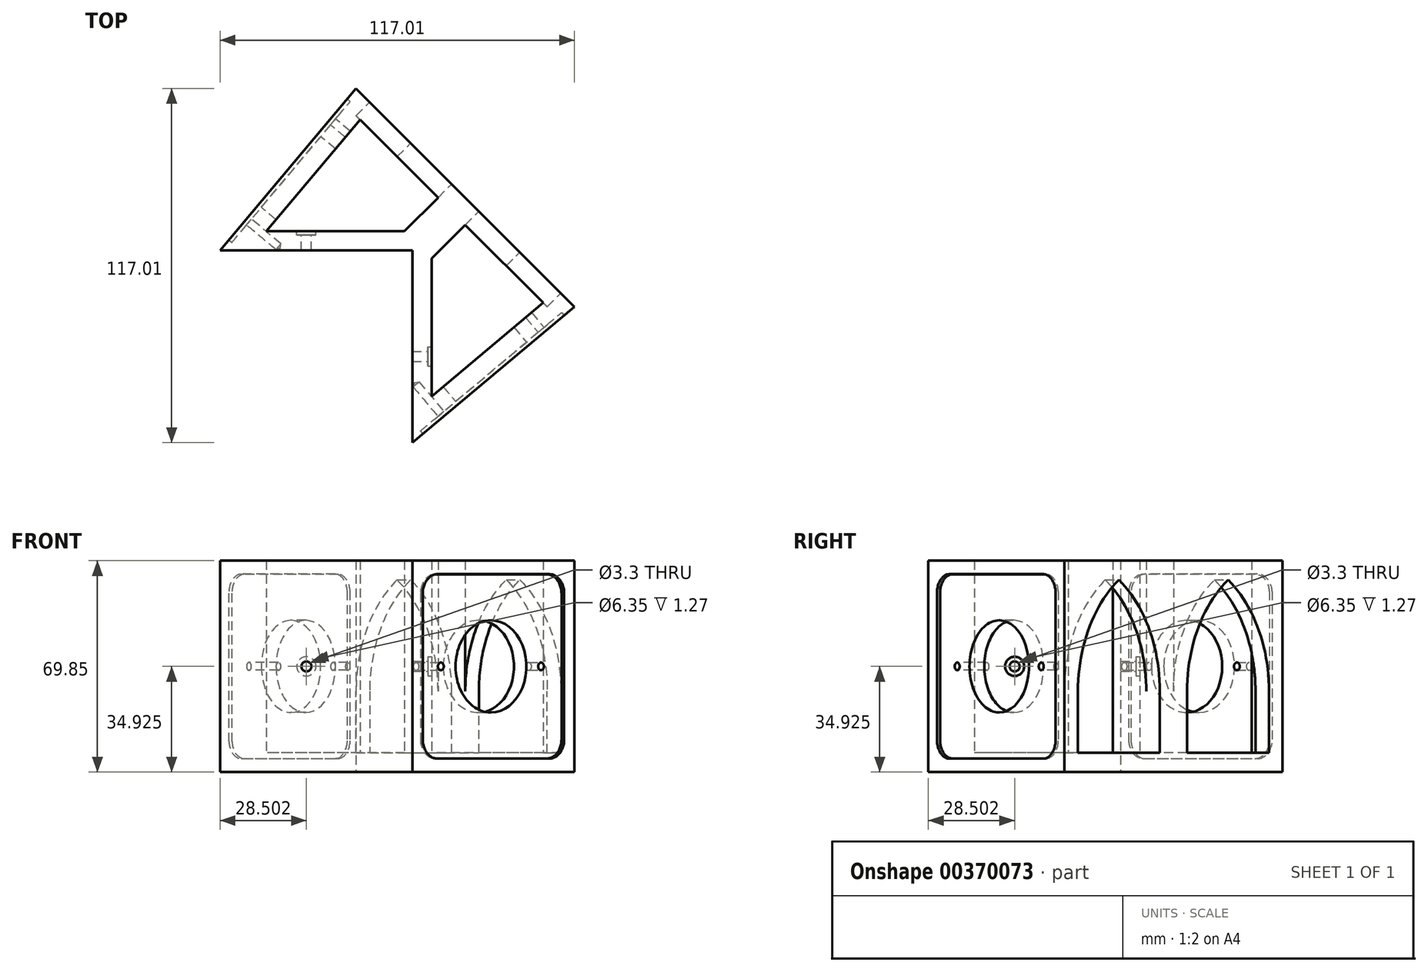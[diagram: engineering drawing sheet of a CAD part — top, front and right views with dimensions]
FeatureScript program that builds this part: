
annotation { "Feature Type Name" : "Feature", "Feature Type Description" : "" }
export const myFeature = defineFeature(function(context is Context, id is Id, definition is map)
    precondition{}
    {
        {
            var Q0;
            Q0=qCreatedBy(makeId("Top.planeOp"),FACE);
            var sketch = newSketch(context, id + "F0", { "sketchPlane" : qUnion([Q0])});
            skLineSegment(sketch, "E0", {"start": v(0, 0) * mm, "end": v(0, 63.5) * mm});
            skLineSegment(sketch, "E1", {"start": v(0, 63.5) * mm, "end": v(53.5, 18.6) * mm});
            skLineSegment(sketch, "E2", {"start": v(0, 0) * mm, "end": v(17.45, -17.45) * mm});
            skLineSegment(sketch, "E3", {"start": v(17.45, -17.45) * mm, "end": v(53.5, 18.6) * mm});
            skSolve(sketch);
        }
        {
            var Q0;
            Q0 = qSketchRegion(id + "F0", true);
            extrude(context, id + "F1", {"entities" : qUnion([Q0]), "oppositeDirection" : true, "depth" : 69.85 * mm});
        }
        {
            var Q0;
            Q0=makeQuery(id+"F1.opExtrude","SWEPT_FACE",FACE,{"disambiguationData":[OSD([sQuery(id+"F0.wireOp",EDGE,"E1")])]});
            var sketch = newSketch(context, id + "F2", { "sketchPlane" : qUnion([Q0])});
            skLineSegment(sketch, "E4", {"start": v(-18.24, -65.4) * mm, "end": v(30.02, -65.4) * mm});
            skLineSegment(sketch, "E5", {"start": v(36.37, -59.06) * mm, "end": v(36.37, -10.8) * mm});
            skLineSegment(sketch, "E6", {"start": v(30.02, -4.45) * mm, "end": v(-18.24, -4.45) * mm});
            skLineSegment(sketch, "E7", {"start": v(-24.59, -10.8) * mm, "end": v(-24.59, -59.06) * mm});
            skArc(sketch, "E8", {"start": v(30.02, -65.4) * mm, "mid": v(34.51, -63.55) * mm, "end": v(36.37, -59.06) * mm});
            skArc(sketch, "E9", {"start": v(36.37, -10.8) * mm, "mid": v(34.51, -6.3) * mm, "end": v(30.02, -4.44) * mm});
            skArc(sketch, "E10", {"start": v(-18.24, -4.44) * mm, "mid": v(-22.73, -6.3) * mm, "end": v(-24.59, -10.8) * mm});
            skArc(sketch, "E11", {"start": v(-24.59, -59.06) * mm, "mid": v(-22.73, -63.55) * mm, "end": v(-18.24, -65.4) * mm});
            skLineSegment(sketch, "E12", {"start": v(5.9, -65.4) * mm, "end": v(5.9, -69.85) * mm, "construction": true});
            skLineSegment(sketch, "E13", {"start": v(-24.59, -34.93) * mm, "end": v(-29.03, -34.93) * mm, "construction": true});
            skLineSegment(sketch, "E14", {"start": v(5.9, -4.45) * mm, "end": v(5.9, 0) * mm, "construction": true});
            skLineSegment(sketch, "E15", {"start": v(36.37, -34.93) * mm, "end": v(40.82, -34.93) * mm, "construction": true});
            skSolve(sketch);
        }
        {
            var Q0;
            Q0=makeQuery(id+"F2.imprint","IMPRINT",FACE,{"disambiguationData":[TD([[makeQuery(id+"F2.imprint","IMPRINT",EDGE,{"derivedFrom":sQuery(id+"F2.wireOp",EDGE,"E4")}),1.0]])]});
            extrude(context, id + "F3", {"entities" : qUnion([Q0]), "operationType" : NewBodyOperationType.REMOVE, "oppositeDirection" : true, "depth" : 1.27 * mm, "hasDraft" : true, "draftAngle" : 3 * degree, "draftPullDirection" : true});
        }
        {
            var Q0;
            Q0=makeQuery(id+"F1.opExtrude","CAP_FACE",FACE,{"disambiguationData":[OSD([sQuery(id+"F0.wireOp",EDGE,"E0"),sQuery(id+"F0.wireOp",EDGE,"E1"),sQuery(id+"F0.wireOp",EDGE,"E2"),sQuery(id+"F0.wireOp",EDGE,"E3")])],"isStart":false});
            shell(context, id + "F4", {"entities" : qUnion([Q0]), "thickness" : 6.35 * mm});
        }
        {
            var Q0;
            Q0=makeQuery(id+"F1.opExtrude","SWEPT_FACE",FACE,{"disambiguationData":[OSD([sQuery(id+"F0.wireOp",EDGE,"E3")])]});
            var sketch = newSketch(context, id + "F5", { "sketchPlane" : qUnion([Q0])});
            skLineSegment(sketch, "E16", {"start": v(6.35, -6.35) * mm, "end": v(6.35, -63.5) * mm});
            skLineSegment(sketch, "E17", {"start": v(6.35, -63.5) * mm, "end": v(44.64, -63.5) * mm});
            skLineSegment(sketch, "E18", {"start": v(44.64, -63.5) * mm, "end": v(44.64, -6.35) * mm});
            skLineSegment(sketch, "E19", {"start": v(44.64, -6.35) * mm, "end": v(6.35, -6.35) * mm});
            skLineSegment(sketch, "E20", {"start": v(25.5, -6.35) * mm, "end": v(25.5, 0) * mm, "construction": true});
            skLineSegment(sketch, "E21", {"start": v(44.64, -34.93) * mm, "end": v(50.99, -34.93) * mm, "construction": true});
            skLineSegment(sketch, "E22", {"start": v(25.5, -63.5) * mm, "end": v(25.5, -69.85) * mm, "construction": true});
            skLineSegment(sketch, "E23", {"start": v(6.35, -34.93) * mm, "end": v(0, -34.93) * mm, "construction": true});
            skArc(sketch, "E24", {"start": v(25.5, -63.5) * mm, "mid": v(39.57, -47.43) * mm, "end": v(44.64, -26.68) * mm});
            skArc(sketch, "E25.MirrorCS", {"start": v(25.5, -63.5) * mm, "mid": v(11.42, -47.43) * mm, "end": v(6.35, -26.68) * mm});
            skSolve(sketch);
        }
        {
            var Q0;
            {var subQ1=sQuery(id+"F5.wireOp",EDGE,"E19");Q0=makeQuery(id+"F5.imprint","IMPRINT",FACE,{"disambiguationData":[TD([[makeQuery(id+"F5.imprint","IMPRINT",EDGE,{"derivedFrom":subQ1}),1.0]])]});}
            var Q1;
            Q1=makeQuery(id+"F4.opShell","OFFSET_FACE",FACE,{"disambiguationData":[OSD([sQuery(id+"F0.wireOp",EDGE,"E3")]),OD(0.0)]});
            extrude(context, id + "F6", {"entities" : qUnion([Q0]), "operationType" : NewBodyOperationType.REMOVE, "endBound" : BoundingType.UP_TO_SURFACE, "oppositeDirection" : true, "endBoundEntityFace" : qUnion([Q1]), "depth" : 25.4 * mm});
        }
        {
            var Q0;
            Q0=makeQuery(id+"F3.boolean.opBoolean","COPY",FACE,{"derivedFrom":makeQuery(id+"F3.opExtrude","CAP_FACE",FACE,{"disambiguationData":[OSD([sQuery(id+"F2.wireOp",EDGE,"E4"),sQuery(id+"F2.wireOp",EDGE,"E5"),sQuery(id+"F2.wireOp",EDGE,"E6"),sQuery(id+"F2.wireOp",EDGE,"E7"),sQuery(id+"F2.wireOp",EDGE,"E8"),sQuery(id+"F2.wireOp",EDGE,"E9"),sQuery(id+"F2.wireOp",EDGE,"E10"),sQuery(id+"F2.wireOp",EDGE,"E11")])],"isStart":false})});
            var sketch = newSketch(context, id + "F7", { "sketchPlane" : qUnion([Q0])});
            skLineSegment(sketch, "E26", {"start": v(27.48, -34.93) * mm, "end": v(-15.7, -34.93) * mm, "construction": true});
            skPoint(sketch, "E27", {"position": v(-15.7, -34.92) * mm});
            skPoint(sketch, "E28", {"position": v(27.48, -34.92) * mm});
            skLineSegment(sketch, "E29", {"start": v(27.48, -34.93) * mm, "end": v(36.3, -34.93) * mm, "construction": true});
            skLineSegment(sketch, "E30", {"start": v(-15.7, -34.93) * mm, "end": v(-24.52, -34.93) * mm, "construction": true});
            skCircle(sketch, "E31", {"center": v(5.9, -34.92) * mm, "radius": 15.24 * mm});
            skSolve(sketch);
        }
        {
            var Q0;
            Q0=sQuery(id+"F7.wireOp",VERTEX,"E28");
            var Q1;
            Q1=sQuery(id+"F7.wireOp",VERTEX,"E27");
            var Q2;
            Q2=makeQuery(id+"F1.opExtrude","SWEPT_BODY",BODY,{"disambiguationData":[OSD([sQuery(id+"F0.wireOp",EDGE,"E0"),sQuery(id+"F0.wireOp",EDGE,"E1"),sQuery(id+"F0.wireOp",EDGE,"E2"),sQuery(id+"F0.wireOp",EDGE,"E3")])]});
            hole(context, id + "F8", {"style" : HoleStyle.SIMPLE, "endStyle" : HoleEndStyle.BLIND, "holeDiameter" : 2.54 * mm, "holeDepth" : 12.7 * mm, "isTappedThrough" : true, "tappedDepth" : 12.7 * mm, "tapClearance" : 3, "locations" : qUnion([Q0, Q1]), "scope" : qUnion([Q2])});
        }
        {
            var Q0;
            Q0=makeQuery(id+"F7.imprint","IMPRINT",FACE,{"disambiguationData":[TD([[makeQuery(id+"F7.imprint","IMPRINT",EDGE,{"derivedFrom":sQuery(id+"F7.wireOp",EDGE,"E31")}),1.0]])]});
            extrude(context, id + "F9", {"entities" : qUnion([Q0]), "operationType" : NewBodyOperationType.REMOVE, "endBound" : BoundingType.UP_TO_NEXT, "oppositeDirection" : true, "depth" : 25.4 * mm});
        }
        {
            var Q0;
            Q0=makeQuery(id+"F4.opShell","OFFSET_FACE",FACE,{"disambiguationData":[OSD([sQuery(id+"F0.wireOp",EDGE,"E0")])]});
            var sketch = newSketch(context, id + "F10", { "sketchPlane" : qUnion([Q0])});
            skPoint(sketch, "E32", {"position": v(40.08, -34.92) * mm});
            skLineSegment(sketch, "E33", {"start": v(40.08, -34.92) * mm, "end": v(35, -34.92) * mm, "construction": true});
            skPoint(sketch, "E34", {"position": v(35, -34.92) * mm});
            skSolve(sketch);
        }
        {
            var Q0;
            Q0=sQuery(id+"F10.wireOp",VERTEX,"E34");
            var Q1;
            Q1=makeQuery(id+"F1.opExtrude","SWEPT_BODY",BODY,{"disambiguationData":[OSD([sQuery(id+"F0.wireOp",EDGE,"E0"),sQuery(id+"F0.wireOp",EDGE,"E1"),sQuery(id+"F0.wireOp",EDGE,"E2"),sQuery(id+"F0.wireOp",EDGE,"E3")])]});
            hole(context, id + "F11", {"style" : HoleStyle.C_BORE, "endStyle" : HoleEndStyle.BLIND, "holeDiameter" : 3.3 * mm, "cBoreDiameter" : 6.35 * mm, "cBoreDepth" : 1.27 * mm, "holeDepth" : 12.7 * mm, "isTappedThrough" : true, "tappedDepth" : 12.7 * mm, "tapClearance" : 3, "locations" : qUnion([Q0]), "scope" : qUnion([Q1])});
        }
        {
            var Q0;
            Q0=makeQuery(id+"F1.opExtrude","SWEPT_BODY",BODY,{"disambiguationData":[OSD([sQuery(id+"F0.wireOp",EDGE,"E0"),sQuery(id+"F0.wireOp",EDGE,"E1"),sQuery(id+"F0.wireOp",EDGE,"E2"),sQuery(id+"F0.wireOp",EDGE,"E3")])]});
            var Q1;
            Q1=makeQuery(id+"F1.opExtrude","SWEPT_FACE",FACE,{"disambiguationData":[OSD([sQuery(id+"F0.wireOp",EDGE,"E2")])]});
            mirror(context, id + "F12", {"operationType" : NewBodyOperationType.ADD, "entities" : qUnion([Q0]), "mirrorPlane" : qUnion([Q1])});
        }
        {
            var Q0;
            Q0=makeQuery(id+"F1.opExtrude","SWEPT_BODY",BODY,{"disambiguationData":[OSD([sQuery(id+"F0.wireOp",EDGE,"E0"),sQuery(id+"F0.wireOp",EDGE,"E1"),sQuery(id+"F0.wireOp",EDGE,"E2"),sQuery(id+"F0.wireOp",EDGE,"E3")])]});
            var Q1;
            Q1=makeQuery(id+"F12.opPattern","COPY",EDGE,{"derivedFrom":makeQuery(id+"F1.opExtrude","CAP_EDGE",EDGE,{"disambiguationData":[OSD([sQuery(id+"F0.wireOp",EDGE,"E0")])],"isStart":true}),"instanceName":"1"});
            transform(context, id + "F13", {"entities" : qUnion([Q0]), "transformType" : TransformType.ROTATION, "transformAxis" : qUnion([Q1]), "angle" : 180 * degree, "makeCopy" : false});
        }
    });
